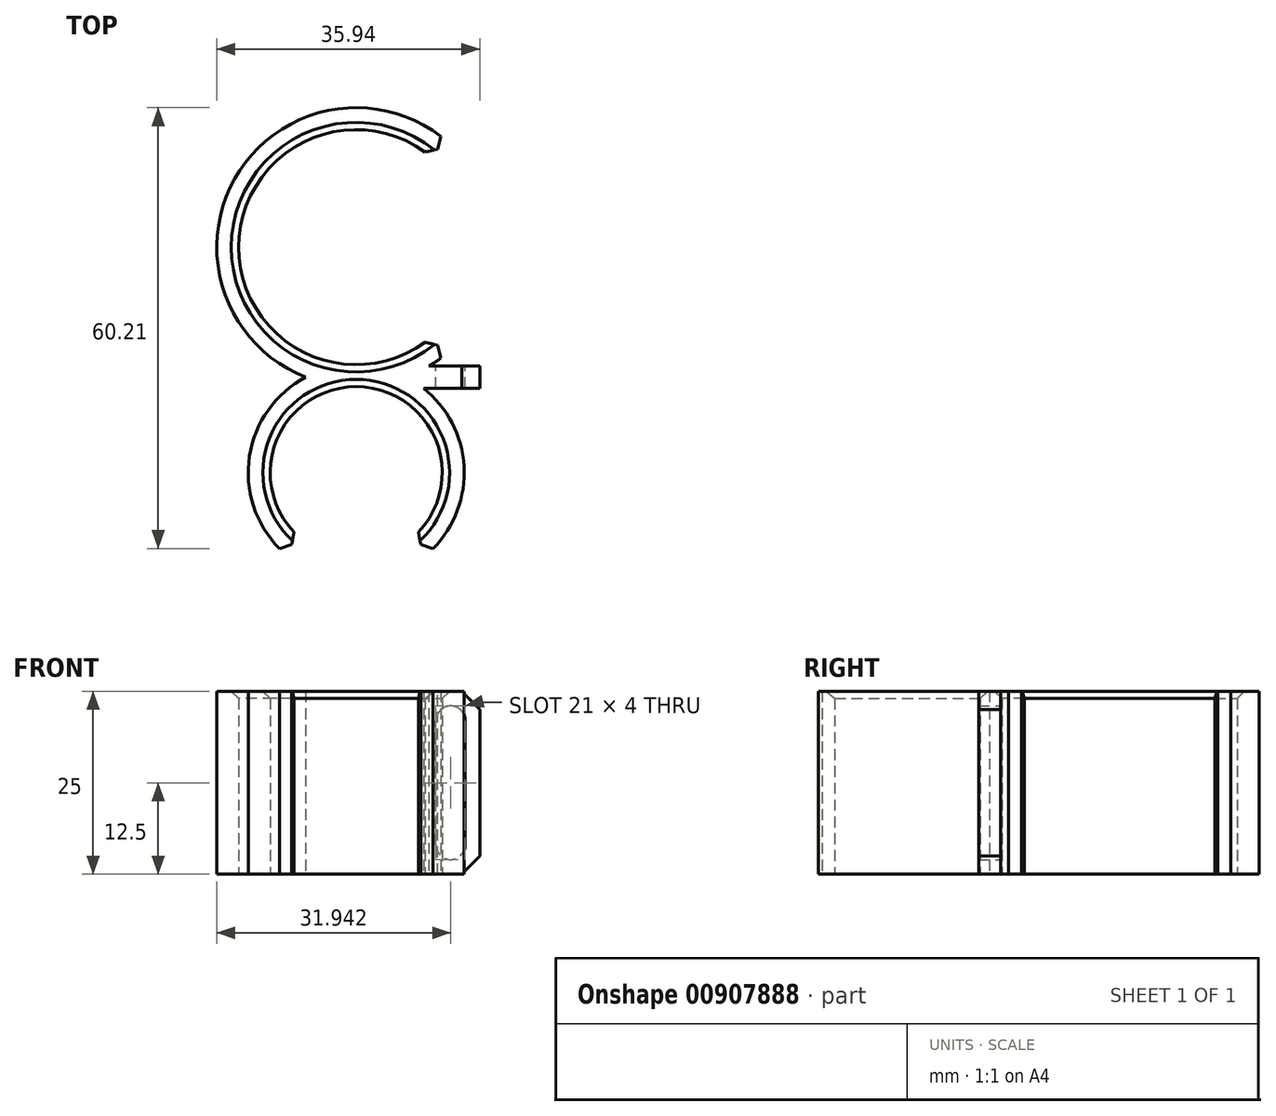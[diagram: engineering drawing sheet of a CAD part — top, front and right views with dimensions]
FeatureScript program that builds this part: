
annotation { "Feature Type Name" : "Feature", "Feature Type Description" : "" }
export const myFeature = defineFeature(function(context is Context, id is Id, definition is map)
    precondition{}
    {
        {
            var Q0;
            Q0=qCreatedBy(makeId("Top.planeOp"),FACE);
            var sketch = newSketch(context, id + "F0", { "sketchPlane" : qUnion([Q0])});
            skArc(sketch, "E0", {"start": v(9.41, 13) * mm, "mid": v(-16.05, 0) * mm, "end": v(9.41, -13) * mm});
            skArc(sketch, "E1", {"start": v(13.11, 13.82) * mm, "mid": v(-16.1, 10.2) * mm, "end": v(-6.9, -17.76) * mm});
            skLineSegment(sketch, "E2", {"start": v(0, 0) * mm, "end": v(41.14, 0) * mm, "construction": true});
            skLineSegment(sketch, "E3", {"start": v(9.41, 13) * mm, "end": v(13.11, 13.82) * mm});
            skLineSegment(sketch, "E4", {"start": v(9.41, -13) * mm, "end": v(13.11, -13.82) * mm});
            skArc(sketch, "E5.trimOffspring", {"start": v(6.9, -17.76) * mm, "mid": v(10.2, -16.1) * mm, "end": v(13.11, -13.82) * mm});
            skArc(sketch, "E6", {"start": v(8.5, -38.91) * mm, "mid": v(0, -19.05) * mm, "end": v(-8.5, -38.91) * mm});
            skArc(sketch, "E7", {"start": v(-6.9, -17.76) * mm, "mid": v(-14.7, -29.48) * mm, "end": v(-9.11, -42.4) * mm});
            skLineSegment(sketch, "E8", {"start": v(0, -30.8) * mm, "end": v(0, -49.73) * mm, "construction": true});
            skPoint(sketch, "E8.endSnap0", {"position": v(0, -45.55) * mm});
            skLineSegment(sketch, "E9", {"start": v(-8.5, -38.91) * mm, "end": v(-9.11, -42.4) * mm});
            skLineSegment(sketch, "E10", {"start": v(8.5, -38.91) * mm, "end": v(9.11, -42.4) * mm});
            skArc(sketch, "E11.trimOffspring", {"start": v(9.11, -42.4) * mm, "mid": v(14.7, -29.48) * mm, "end": v(6.9, -17.76) * mm});
            skSolve(sketch);
        }
        {
            var Q0;
            Q0 = qSketchRegion(id + "F0", true);
            extrude(context, id + "F1", {"entities" : qUnion([Q0]), "depth" : 25 * mm, "offsetDistance" : 25 * mm});
        }
        {
            var Q0;
            Q0=qCreatedBy(makeId("Front.planeOp"),FACE);
            var Q1;
            Q1=makeQuery(id+"F1.opExtrude","CAP_VERTEX",VERTEX,{"disambiguationData":[OSD([sQuery(id+"F0.wireOp",EDGE,"E5.trimOffspring"),sQuery(id+"F0.wireOp",EDGE,"E11.trimOffspring")])],"isStart":false});
            cPlane(context, id + "F2", {"entities" : qUnion([Q0, Q1]), "cplaneType" : CPlaneType.PLANE_POINT, "offset" : 25 * mm, "width" : 150 * mm, "height" : 150 * mm});
        }
        {
            var Q0;
            Q0=qCreatedBy(id+"F2.planeOp",FACE);
            var sketch = newSketch(context, id + "F3", { "sketchPlane" : qUnion([Q0])});
            skLineSegment(sketch, "E12.0", {"start": v(6.9, 25) * mm, "end": v(6.9, 0) * mm});
            skLineSegment(sketch, "E13", {"start": v(6.9, 25) * mm, "end": v(16.9, 25) * mm});
            skLineSegment(sketch, "E14", {"start": v(16.9, 25) * mm, "end": v(16.9, 0) * mm});
            skLineSegment(sketch, "E15", {"start": v(16.9, 0) * mm, "end": v(6.9, 0) * mm});
            skLineSegment(sketch, "E16", {"start": v(12.9, 25) * mm, "end": v(12.9, 0) * mm, "construction": true});
            skArc(sketch, "E17", {"start": v(14.9, 21) * mm, "mid": v(12.9, 23) * mm, "end": v(10.9, 21) * mm});
            skArc(sketch, "E18", {"start": v(10.9, 4) * mm, "mid": v(12.9, 2) * mm, "end": v(14.9, 4) * mm});
            skLineSegment(sketch, "E19", {"start": v(14.9, 21) * mm, "end": v(14.9, 4) * mm});
            skLineSegment(sketch, "E20", {"start": v(10.9, 4) * mm, "end": v(10.9, 21) * mm});
            skLineSegment(sketch, "E21", {"start": v(16.9, 12.5) * mm, "end": v(6.9, 12.5) * mm, "construction": true});
            skSolve(sketch);
        }
        {
            var Q0;
            Q0 = qSketchRegion(id + "F3", true);
            extrude(context, id + "F4", {"entities" : qUnion([Q0]), "operationType" : NewBodyOperationType.ADD, "endBound" : BoundingType.SYMMETRIC, "depth" : 3 * mm, "offsetDistance" : 25 * mm});
        }
        {
            var Q0;
            Q0=makeQuery(id+"FQxxyLi2HCBFLKR_1.1.F4.opExtrude","SWEPT_EDGE",EDGE,{"disambiguationData":[OSD([sQuery(id+"F3.wireOp",EDGE,"E14"),sQuery(id+"F3.wireOp",EDGE,"E15")])]});
            var Q1;
            Q1=makeQuery(id+"FQxxyLi2HCBFLKR_1.1.F4.opExtrude","SWEPT_EDGE",EDGE,{"disambiguationData":[OSD([sQuery(id+"F3.wireOp",EDGE,"E13"),sQuery(id+"F3.wireOp",EDGE,"E14")])]});
            var Q2;
            Q2=makeQuery(id+"F4.opExtrude","SWEPT_EDGE",EDGE,{"disambiguationData":[OSD([sQuery(id+"F3.wireOp",EDGE,"E14"),sQuery(id+"F3.wireOp",EDGE,"E15")])]});
            var Q3;
            Q3=makeQuery(id+"F4.opExtrude","SWEPT_EDGE",EDGE,{"disambiguationData":[OSD([sQuery(id+"F3.wireOp",EDGE,"E13"),sQuery(id+"F3.wireOp",EDGE,"E14")])]});
            chamfer(context, id + "F5", {"entities" : qUnion([Q0, Q1, Q2, Q3]), "width" : 2.5 * mm, "tangentPropagation" : true});
        }
        {
            var Q0;
            Q0=makeQuery(id+"F1.opExtrude","SWEPT_EDGE",EDGE,{"disambiguationData":[OSD([sQuery(id+"F0.wireOp",EDGE,"E1"),sQuery(id+"F0.wireOp",EDGE,"E3")])]});
            var Q1;
            Q1=makeQuery(id+"F1.opExtrude","SWEPT_EDGE",EDGE,{"disambiguationData":[OSD([sQuery(id+"F0.wireOp",EDGE,"E4"),sQuery(id+"F0.wireOp",EDGE,"E5.trimOffspring")])]});
            var Q2;
            Q2=makeQuery(id+"F1.opExtrude","SWEPT_EDGE",EDGE,{"disambiguationData":[OSD([sQuery(id+"F0.wireOp",EDGE,"E7"),sQuery(id+"F0.wireOp",EDGE,"E9")])]});
            var Q3;
            Q3=makeQuery(id+"F1.opExtrude","SWEPT_EDGE",EDGE,{"disambiguationData":[OSD([sQuery(id+"F0.wireOp",EDGE,"E10"),sQuery(id+"F0.wireOp",EDGE,"E11.trimOffspring")])]});
            var Q4;
            Q4=makeQuery(id+"F1.opExtrude","CAP_EDGE",EDGE,{"disambiguationData":[OSD([sQuery(id+"F0.wireOp",EDGE,"E6")])],"isStart":false});
            var Q5;
            Q5=makeQuery(id+"F1.opExtrude","CAP_EDGE",EDGE,{"disambiguationData":[OSD([sQuery(id+"F0.wireOp",EDGE,"E0")])],"isStart":false});
            chamfer(context, id + "F6", {"entities" : qUnion([Q0, Q1, Q2, Q3, Q4, Q5]), "width" : 1 * mm, "tangentPropagation" : true});
        }
    });
